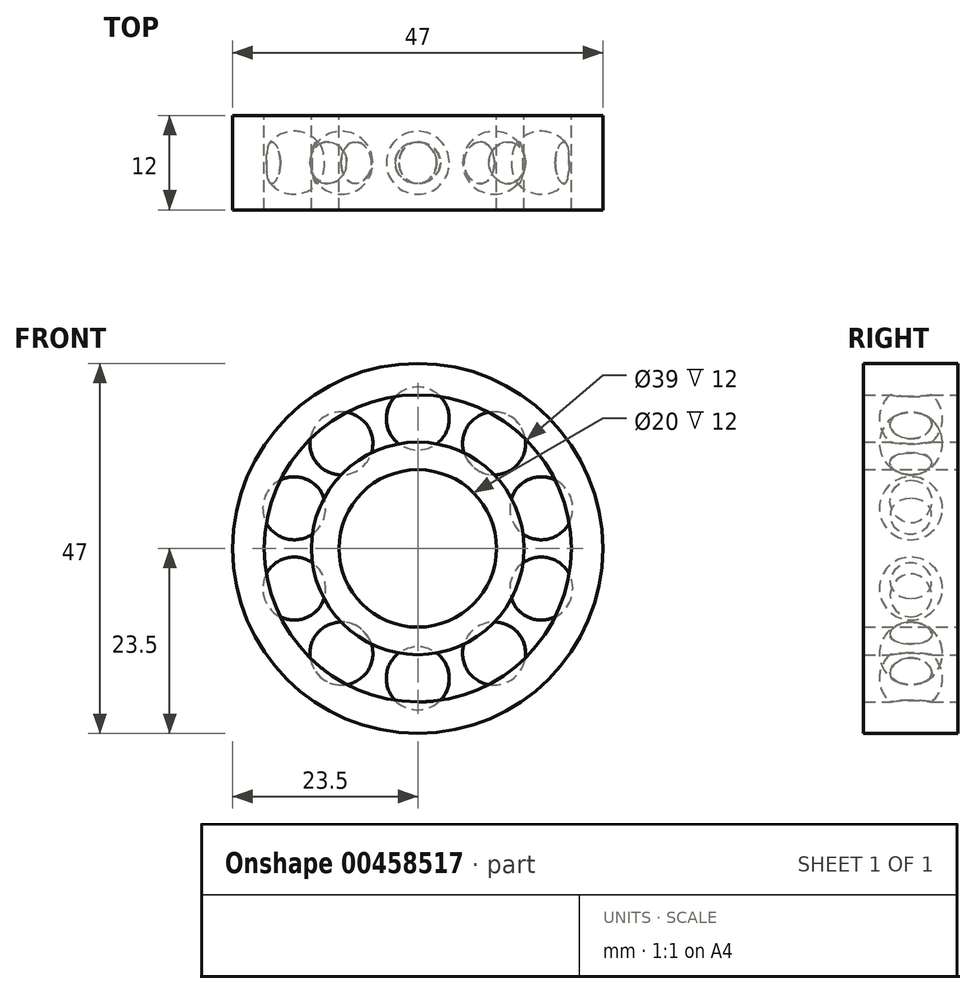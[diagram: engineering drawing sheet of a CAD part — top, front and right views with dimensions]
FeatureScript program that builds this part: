
annotation { "Feature Type Name" : "Feature", "Feature Type Description" : "" }
export const myFeature = defineFeature(function(context is Context, id is Id, definition is map)
    precondition{}
    {
        {
            var Q0;
            Q0=qCreatedBy(makeId("Front.planeOp"),FACE);
            var sketch = newSketch(context, id + "F0", { "sketchPlane" : qUnion([Q0])});
            skCircle(sketch, "E0", {"center": v(0, 0) * mm, "radius": 19.5 * mm});
            skCircle(sketch, "E1", {"center": v(0, 0) * mm, "radius": 23.5 * mm});
            skCircle(sketch, "E2", {"center": v(0, 0) * mm, "radius": 10 * mm});
            skCircle(sketch, "E3", {"center": v(0, 0) * mm, "radius": 13.5 * mm});
            skSolve(sketch);
        }
        {
            var Q0;
            Q0=makeQuery(id+"F0.imprint","IMPRINT",FACE,{"disambiguationData":[TD([[makeQuery(id+"F0.imprint","IMPRINT",EDGE,{"derivedFrom":sQuery(id+"F0.wireOp",EDGE,"E2")}),-1.0]])]});
            var Q1;
            Q1=makeQuery(id+"F0.imprint","IMPRINT",FACE,{"disambiguationData":[TD([[makeQuery(id+"F0.imprint","IMPRINT",EDGE,{"derivedFrom":sQuery(id+"F0.wireOp",EDGE,"E0")}),-1.0]])]});
            extrude(context, id + "F1", {"entities" : qUnion([Q0, Q1]), "depth" : 12 * mm, "symmetric" : true});
        }
        {
            var Q0;
            Q0=qCreatedBy(makeId("Front.planeOp"),FACE);
            var sketch = newSketch(context, id + "F2", { "sketchPlane" : qUnion([Q0])});
            skArc(sketch, "E4", {"start": v(0, 12.5) * mm, "mid": v(4, 16.5) * mm, "end": v(0, 20.5) * mm});
            skLineSegment(sketch, "E5", {"start": v(0, 20.5) * mm, "end": v(0, 12.5) * mm});
            skSolve(sketch);
        }
        {
            var Q0;
            Q0=makeQuery(id+"F2.imprint","IMPRINT",FACE,{"disambiguationData":[TD([[makeQuery(id+"F2.imprint","IMPRINT",EDGE,{"derivedFrom":sQuery(id+"F2.wireOp",EDGE,"E4")}),1.0]])]});
            var Q1;
            Q1=sQuery(id+"F2.wireOp",EDGE,"E5");
            revolve(context, id + "F3", {"entities" : qUnion([Q0]), "axis" : qUnion([Q1]), "revolveType" : RevolveType.FULL});
        }
        {
            var Q0;
            Q0=makeQuery(id+"F3.opRevolve","SWEPT_BODY",BODY,{"disambiguationData":[OSD([sQuery(id+"F2.wireOp",EDGE,"E4"),sQuery(id+"F2.wireOp",EDGE,"E5")])]});
            var Q1;
            Q1=makeQuery(id+"F1.opExtrude","SWEPT_FACE",FACE,{"disambiguationData":[OSD([sQuery(id+"F0.wireOp",EDGE,"E3")])]});
            circularPattern(context, id + "F4", {"operationType" : NewBodyOperationType.ADD, "entities" : qUnion([Q0]), "axis" : qUnion([Q1]), "angle" : 360 * degree, "instanceCount" : 10, "equalSpace" : true});
        }
    });
